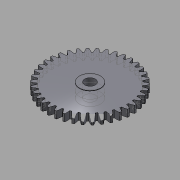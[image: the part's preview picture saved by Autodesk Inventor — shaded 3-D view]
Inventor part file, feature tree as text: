
AUTODESK INVENTOR PART (.ipt)
format: ipt  version: 2015 (Build 190159000, 159)  size: 348,672 bytes
history: native  units: in
note: dims shown in document units (in); Inventor stores cm internally (conversion verified against a paired STEP export)
features: other x13, sketch x5, plane x2
ambient origin geometry x8: Origin, YZ Plane, XZ Plane, XY Plane, X Axis, Y Axis, Z Axis, Center Point
bodies: Solid1 (feature_tree)
feature tree (20):
  other  "Spur Gear28_MIR4.ipt"
  other  "Solid1::Spur Gear28_MIR4.ipt"
  other  "TaggingFeature1"
  sketch  "Sketch1"  dims[d0=0.3937in]
  sketch  "Sketch2"  dims[d16=0.5709in d17=0.0in d41=0.0in d43=0.5709in d46=0.5709in d47=0.0in d48=0.0in]
  sketch  "Sketch3"
  sketch  "Sketch4"
  sketch  "Sketch5"
  plane  "XZ Plane_1"
  plane  "Work Plane2"
  other  "Z Axis_1"
  other  "Srf1"
  other  "Srf1::Derived"
  other  "Distance iMate"
  other  "Align iMate"
  other  "Mesh iMate"
  other  "Axis iMate"
  other  "Position iMate"
  other  "Mesh iMate2"
  other  "Start plane iMate"
